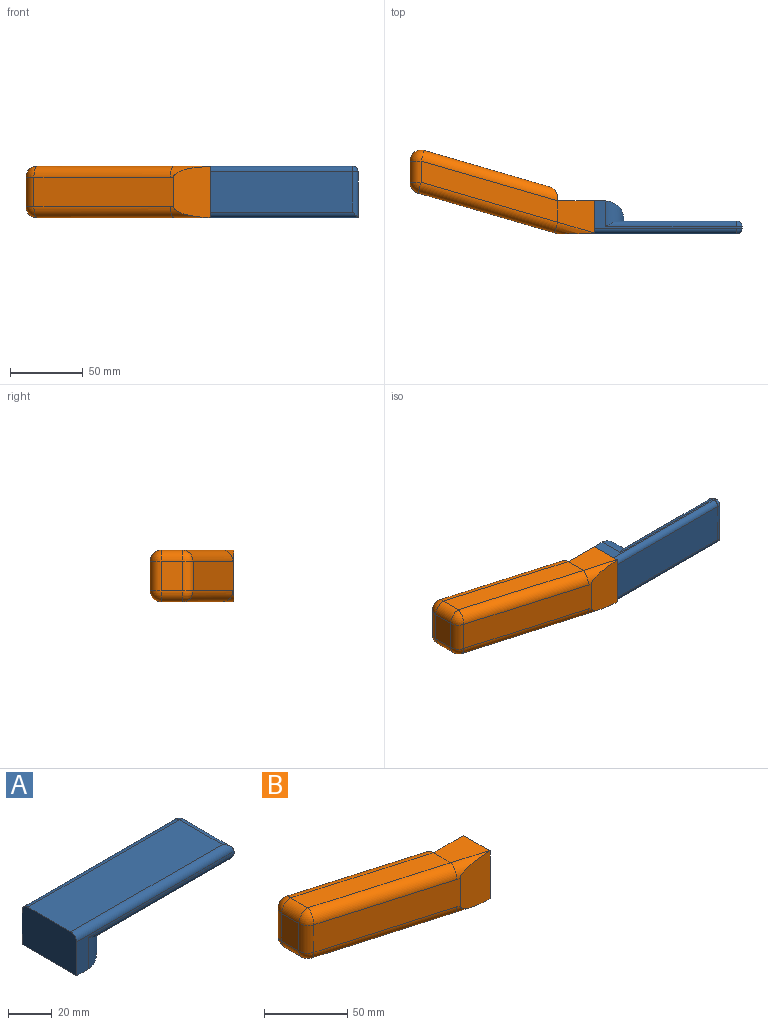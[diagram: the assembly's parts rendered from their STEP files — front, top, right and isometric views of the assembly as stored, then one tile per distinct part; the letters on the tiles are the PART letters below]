
ASSEMBLY  parts=2 mates=1
PART A: 20 faces, bbox 101.6x35.3x22.6 mm
  f0: plane 81.1x27.69mm, normal (0,0,-1), area 2164.9mm2, adj f7,f11,f13,f16,f17,f19
  f1: plane 97.79x18.8mm, normal (0,1,0), area 252.9mm2, adj f5,f6,f10,f14,f16,f19
  f2: plane 97.79x27.69mm, normal (0,0,1), area 2707.4mm2, adj f5,f8,f9,f10
  f3: plane 101.6x18.8mm, normal (0,-1,0), area 257.5mm2, adj f4,f5,f6,f8,f11,f17
  f4: plane 31.5x1.22mm, normal (1,0,0), area 38.3mm2, adj f3,f9,f13,f14
  f5: plane 35.31x22.61mm, normal (-1,0,0), area 791.9mm2, adj f1,f2,f3,f6,f8,f10
  f6: plane 35.31x7.62mm, normal (0,0,-1), area 269mm2, adj f1,f3,f5,f18
  f7: plane 9.91x1.07mm, normal (1,0,0), area 10.6mm2, adj f0,f17,f18,f19
  f8: cylinder r=3.81mm len=101.6mm, axis (1,0,0), area 599.8mm2, adj f2,f3,f5,f9
  f9: cylinder r=3.81mm len=31.5mm, axis (0,1,0), area 180.2mm2, adj f2,f4,f8,f12
  f10: cylinder r=3.81mm len=97.79mm, axis (-1,0,0), area 585.2mm2, adj f1,f2,f5,f12
  f11: cylinder r=3.81mm len=93.98mm, axis (1,0,0), area 524.4mm2, adj f0,f3,f13,f17
  f12: sphere r=3.81mm, area 22.8mm2, adj f9,f10,f14
  f13: cylinder r=3.81mm len=31.5mm, axis (0,-1,0), area 180.2mm2, adj f0,f4,f11,f15
  f14: cylinder r=3.81mm len=3.81mm, axis (0,0,-1), area 7.3mm2, adj f1,f4,f12,f15
  f15: sphere r=3.81mm, area 22.8mm2, adj f13,f14,f16
  f16: cylinder r=3.81mm len=90.17mm, axis (-1,0,0), area 509.9mm2, adj f0,f1,f15,f19
  f17: cylinder r=12.7mm len=17.58mm, axis (0,0,1), area 197.4mm2, adj f0,f3,f7,f11,f18
  f18: cylinder r=12.7mm len=35.31mm, axis (0,-1,0), area 520.2mm2, adj f6,f7,f17,f19
  f19: cylinder r=12.7mm len=17.58mm, axis (0,0,-1), area 197.4mm2, adj f0,f1,f7,f16,f18
PART B: 26 faces, bbox 127.1x64.4x35.5 mm
  f0: plane 35.27x25.4mm, normal (0,-1,0), area 807.8mm2, adj f1,f10,f15,f18
  f1: plane 35.31x22.61mm, normal (1,0,0), area 798.1mm2, adj f0,f2,f3,f4,f15,f18
  f2: plane 35.31x25.4mm, normal (0,1,0), area 896.8mm2, adj f1,f3,f4,f5
  f3: plane 25.4x22.08mm, normal (0,0,-1), area 466.7mm2, adj f1,f2,f9,f15
  f4: plane 25.4x22.08mm, normal (0,0,1), area 466.7mm2, adj f1,f2,f7,f18
  f5: plane 35.31x2.28mm, normal (1,0,0), area 80mm2, adj f2,f7,f9,f11,f12,f14
  f6: plane 20.3x14.62mm, normal (-1,0,0), area 296.7mm2, adj f13,f20,f21,f25
  f7: plane 93.97x42.03mm, normal (0,0,1), area 1379mm2, adj f4,f5,f14,f21,f22
  f8: plane 86.36x25.09mm, normal (0.28,0.96,0), area 1815.9mm2, adj f11,f12,f13,f14
  f9: plane 93.97x42.03mm, normal (0,0,-1), area 1379.1mm2, adj f3,f5,f12,f19,f20
  f10: plane 96.11x28.04mm, normal (-0.28,-0.96,0), area 2020.5mm2, adj f0,f15,f18,f19,f22,f25
  f11: cylinder r=7.62mm len=34.7mm, axis (0,0,1), area 268.9mm2, adj f5,f8,f12,f14
  f12: cylinder r=7.62mm len=96.08mm, axis (0.96,-0.28,0), area 1128.3mm2, adj f5,f8,f9,f11,f16
  f13: cylinder r=7.62mm len=20.3mm, axis (0,0,-1), area 286.7mm2, adj f6,f8,f16,f17
  f14: cylinder r=7.62mm len=96.09mm, axis (-0.96,0.28,0), area 1128.5mm2, adj f5,f7,f8,f11,f17
  f15: cylinder r=7.62mm len=27.69mm, axis (0.96,-0.28,0), area 139.8mm2, adj f0,f1,f3,f10,f19
  f16: sphere r=7.62mm, area 107.7mm2, adj f12,f13,f20
  f17: sphere r=7.62mm, area 107.7mm2, adj f13,f14,f21
  f18: cylinder r=7.62mm len=27.68mm, axis (-0.96,0.28,0), area 139.8mm2, adj f0,f1,f4,f10,f22
  f19: cylinder r=7.62mm len=96.11mm, axis (0.96,-0.28,0), area 1172mm2, adj f9,f10,f15,f23
  f20: cylinder r=7.62mm len=14.62mm, axis (0,1,0), area 175.1mm2, adj f6,f9,f16,f23
  f21: cylinder r=7.62mm len=14.62mm, axis (0,1,0), area 175.1mm2, adj f6,f7,f17,f24
  f22: cylinder r=7.62mm len=96.11mm, axis (-0.96,0.28,0), area 1171.9mm2, adj f7,f10,f18,f24
  f23: sphere r=7.62mm, area 74.9mm2, adj f19,f20,f25
  f24: sphere r=7.62mm, area 74.8mm2, adj f21,f22,f25
  f25: cylinder r=7.62mm len=20.3mm, axis (0,0,1), area 199.1mm2, adj f6,f10,f23,f24
PLACE A rot(axis=(1,0,0),90deg) t=(22.47,-37.2,6.13)mm
PLACE B t=(-2.93,-48.42,23.78)mm
MATE fastened A.f5 <-> B.f1  axis (-1,0,0) through (22.47,-37.12,6.13)mm
